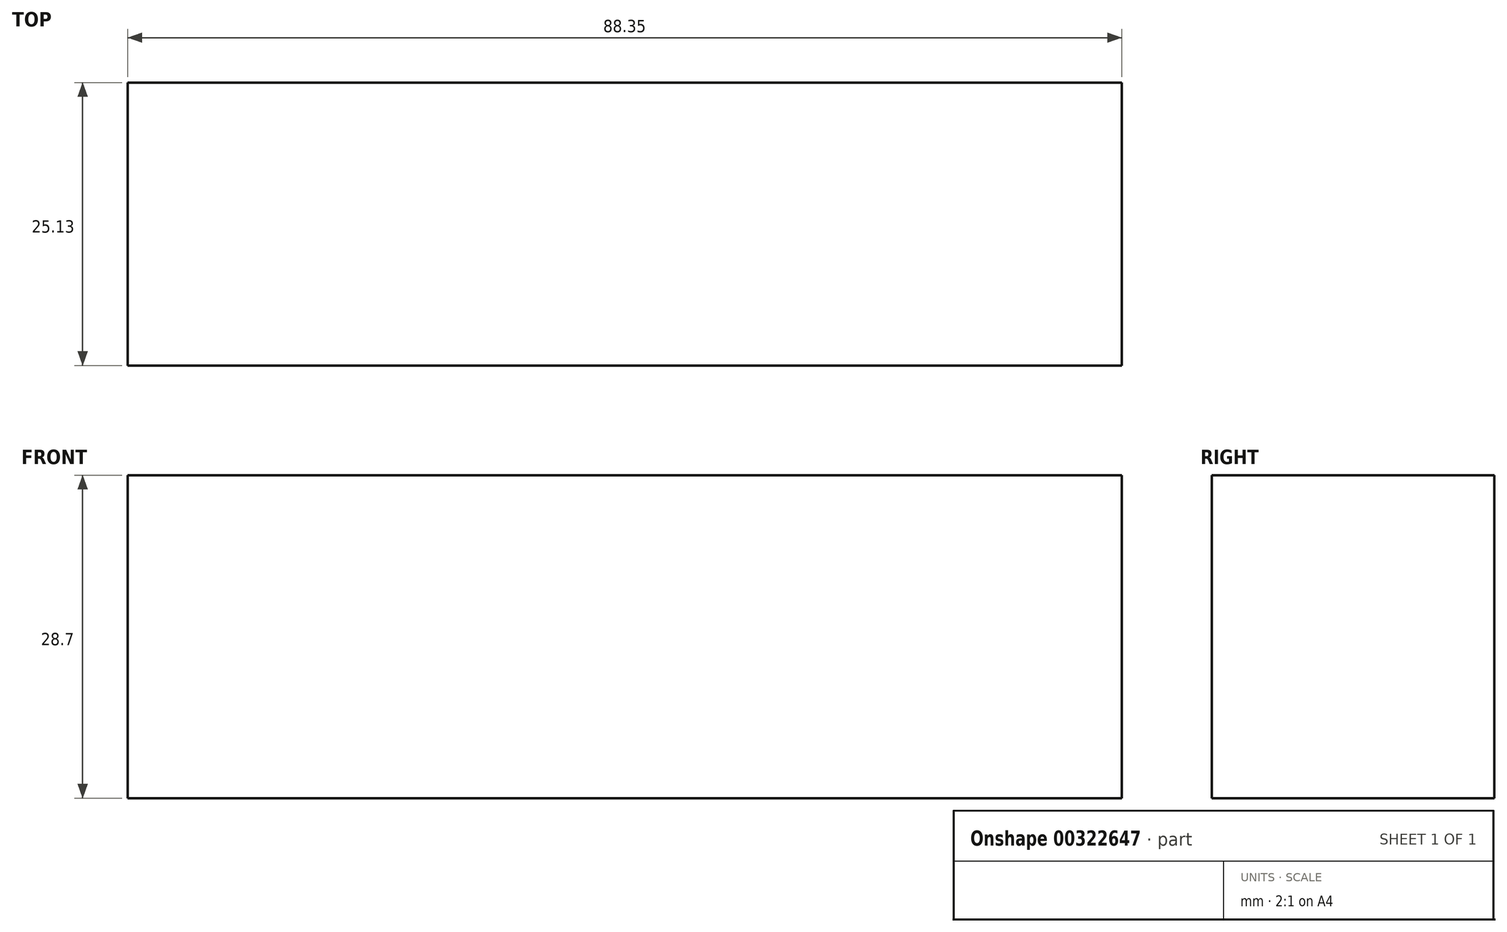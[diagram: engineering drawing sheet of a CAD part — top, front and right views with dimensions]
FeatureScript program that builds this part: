
annotation { "Feature Type Name" : "Feature", "Feature Type Description" : "" }
export const myFeature = defineFeature(function(context is Context, id is Id, definition is map)
    precondition{}
    {
        {
            var Q0;
            Q0=qCreatedBy(makeId("Top.planeOp"),FACE);
            var sketch = newSketch(context, id + "F0", { "sketchPlane" : qUnion([Q0])});
            skLineSegment(sketch, "E0.bottom", {"start": v(-99.19, 55.68) * mm, "end": v(-10.84, 55.68) * mm});
            skLineSegment(sketch, "E0.top", {"start": v(-99.19, 30.55) * mm, "end": v(-10.84, 30.55) * mm});
            skLineSegment(sketch, "E0.left", {"start": v(-99.19, 55.68) * mm, "end": v(-99.19, 30.55) * mm});
            skLineSegment(sketch, "E0.right", {"start": v(-10.84, 55.68) * mm, "end": v(-10.84, 30.55) * mm});
            skSolve(sketch);
        }
        {
            var Q0;
            Q0=makeQuery(id+"F0.imprint","IMPRINT",FACE,{"disambiguationData":[TD([[makeQuery(id+"F0.imprint","IMPRINT",EDGE,{"derivedFrom":sQuery(id+"F0.wireOp",EDGE,"E0.bottom")}),-1.0]])]});
            extrude(context, id + "F1", {"entities" : qUnion([Q0]), "depth" : 28.7 * mm});
        }
    });
